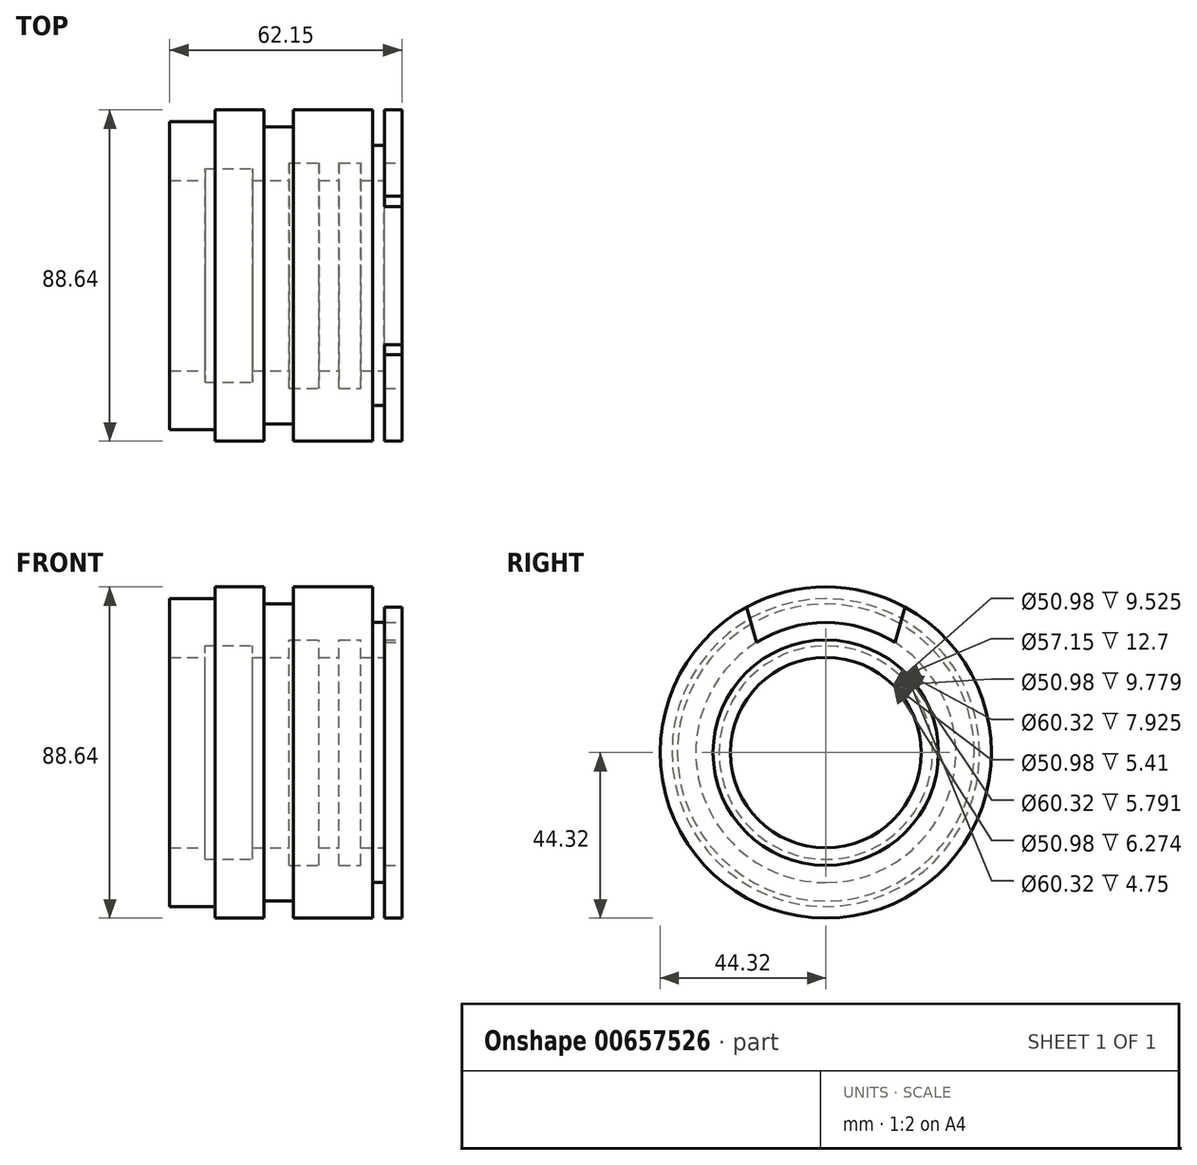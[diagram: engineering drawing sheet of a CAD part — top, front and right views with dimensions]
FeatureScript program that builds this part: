
annotation { "Feature Type Name" : "Feature", "Feature Type Description" : "" }
export const myFeature = defineFeature(function(context is Context, id is Id, definition is map)
    precondition{}
    {
        {
            var Q0;
            Q0=qCreatedBy(makeId("Top.planeOp"),FACE);
            var sketch = newSketch(context, id + "F0", { "sketchPlane" : qUnion([Q0])});
            skLineSegment(sketch, "E0", {"start": v(0, 0) * mm, "end": v(-62.15, 0) * mm});
            skLineSegment(sketch, "E1", {"start": v(-62.15, 0) * mm, "end": v(-62.15, 41.17) * mm});
            skLineSegment(sketch, "E2", {"start": v(-62.15, 41.17) * mm, "end": v(-49.96, 41.17) * mm});
            skLineSegment(sketch, "E3", {"start": v(-49.96, 41.17) * mm, "end": v(-49.96, 44.32) * mm});
            skLineSegment(sketch, "E4", {"start": v(-49.96, 44.32) * mm, "end": v(-36.93, 44.32) * mm});
            skLineSegment(sketch, "E5", {"start": v(-36.93, 44.32) * mm, "end": v(-36.93, 39.75) * mm});
            skLineSegment(sketch, "E6", {"start": v(-36.93, 39.75) * mm, "end": v(-29.03, 39.75) * mm});
            skLineSegment(sketch, "E7", {"start": v(-29.03, 39.75) * mm, "end": v(-29.03, 44.32) * mm});
            skLineSegment(sketch, "E8", {"start": v(-29.03, 44.32) * mm, "end": v(-7.9, 44.32) * mm});
            skLineSegment(sketch, "E9", {"start": v(-7.9, 44.32) * mm, "end": v(-7.9, 34.8) * mm});
            skLineSegment(sketch, "E10", {"start": v(-7.9, 34.8) * mm, "end": v(-4.67, 34.8) * mm});
            skLineSegment(sketch, "E11", {"start": v(-4.67, 34.8) * mm, "end": v(-4.67, 44.32) * mm});
            skLineSegment(sketch, "E12", {"start": v(-4.67, 44.32) * mm, "end": v(0, 44.32) * mm});
            skLineSegment(sketch, "E13", {"start": v(0, 44.32) * mm, "end": v(0, 0) * mm});
            skLineSegment(sketch, "E14", {"start": v(-4.75, 25.49) * mm, "end": v(-11.02, 25.49) * mm});
            skLineSegment(sketch, "E15", {"start": v(-11.02, 25.49) * mm, "end": v(-11.02, 30.16) * mm});
            skLineSegment(sketch, "E16", {"start": v(-11.02, 30.16) * mm, "end": v(-16.81, 30.16) * mm});
            skLineSegment(sketch, "E17", {"start": v(-16.81, 30.16) * mm, "end": v(-16.81, 25.49) * mm});
            skLineSegment(sketch, "E18", {"start": v(-16.81, 25.49) * mm, "end": v(-22.23, 25.49) * mm});
            skLineSegment(sketch, "E19", {"start": v(-22.23, 25.49) * mm, "end": v(-22.23, 30.16) * mm});
            skLineSegment(sketch, "E20", {"start": v(-22.23, 30.16) * mm, "end": v(-30.15, 30.16) * mm});
            skLineSegment(sketch, "E21", {"start": v(-30.15, 30.16) * mm, "end": v(-30.15, 25.49) * mm});
            skLineSegment(sketch, "E22", {"start": v(-30.15, 25.49) * mm, "end": v(-39.93, 25.49) * mm});
            skLineSegment(sketch, "E23", {"start": v(-39.93, 28.58) * mm, "end": v(-39.93, 25.49) * mm});
            skLineSegment(sketch, "E24", {"start": v(0, 30.16) * mm, "end": v(-4.75, 30.16) * mm});
            skLineSegment(sketch, "E25", {"start": v(-4.75, 30.16) * mm, "end": v(-4.75, 25.49) * mm});
            skLineSegment(sketch, "E26", {"start": v(-52.63, 28.57) * mm, "end": v(-52.63, 25.49) * mm});
            skLineSegment(sketch, "E27", {"start": v(-52.63, 28.58) * mm, "end": v(-39.93, 28.58) * mm});
            skLineSegment(sketch, "E28.trimOffspring", {"start": v(-52.63, 25.49) * mm, "end": v(-62.15, 25.49) * mm});
            skPoint(sketch, "E29.orphan", {"position": v(0, 25.49) * mm});
            skSolve(sketch);
        }
        {
            var Q0;
            {var subQ0=sQuery(id+"F0.wireOp",EDGE,"E2");Q0=makeQuery(id+"F0.imprint","IMPRINT",FACE,{"disambiguationData":[TD([[makeQuery(id+"F0.imprint","IMPRINT",EDGE,{"derivedFrom":subQ0}),-1.0]])]});}
            var Q1;
            Q1=sQuery(id+"F0.wireOp",EDGE,"E0");
            revolve(context, id + "F1", {"surfaceOperationType" : NewSurfaceOperationType.NEW, "entities" : qUnion([Q0]), "axis" : qUnion([Q1]), "revolveType" : RevolveType.FULL});
        }
        {
            var Q0;
            Q0=makeQuery(id+"F1.opRevolve","SWEPT_FACE",FACE,{"disambiguationData":[OSD([sQuery(id+"F0.wireOp",EDGE,"E13")])]});
            var sketch = newSketch(context, id + "F2", { "sketchPlane" : qUnion([Q0])});
            skLineSegment(sketch, "E30", {"start": v(0, 30.16) * mm, "end": v(0, 44.32) * mm});
            skLineSegment(sketch, "E31", {"start": v(0, 44.32) * mm, "end": v(-21.2, 44.32) * mm});
            skLineSegment(sketch, "E32", {"start": v(-21.2, 44.32) * mm, "end": v(-21.2, 38.92) * mm});
            skCircle(sketch, "E33", {"center": v(0, 0) * mm, "radius": 34.8 * mm});
            skLineSegment(sketch, "E34", {"start": v(-21.2, 38.92) * mm, "end": v(-18.76, 29.3) * mm});
            skLineSegment(sketch, "E35.MirrorCS", {"start": v(21.2, 38.92) * mm, "end": v(18.76, 29.3) * mm});
            skLineSegment(sketch, "E36", {"start": v(-21.2, 38.92) * mm, "end": v(-18.52, 29.46) * mm});
            skLineSegment(sketch, "E37.MirrorCS", {"start": v(21.2, 38.92) * mm, "end": v(18.52, 29.46) * mm});
            skSolve(sketch);
        }
        {
            var Q0;
            {var subQ5=sQuery(id+"F2.wireOp",EDGE,"E36");Q0=makeQuery(id+"F2.imprint","IMPRINT",FACE,{"disambiguationData":[TD([[makeQuery(id+"F2.imprint","IMPRINT",EDGE,{"derivedFrom":subQ5}),1.0]])]});}
            var Q1;
            {var subQ5=sQuery(id+"F2.wireOp",EDGE,"E37.MirrorCS");Q1=makeQuery(id+"F2.imprint","IMPRINT",FACE,{"disambiguationData":[TD([[makeQuery(id+"F2.imprint","IMPRINT",EDGE,{"derivedFrom":subQ5}),-1.0]])]});}
            extrude(context, id + "F3", {"entities" : qUnion([Q0, Q1]), "operationType" : NewBodyOperationType.REMOVE, "oppositeDirection" : true, "depth" : 4.67 * mm, "offsetDistance" : 25.4 * mm});
        }
    });
